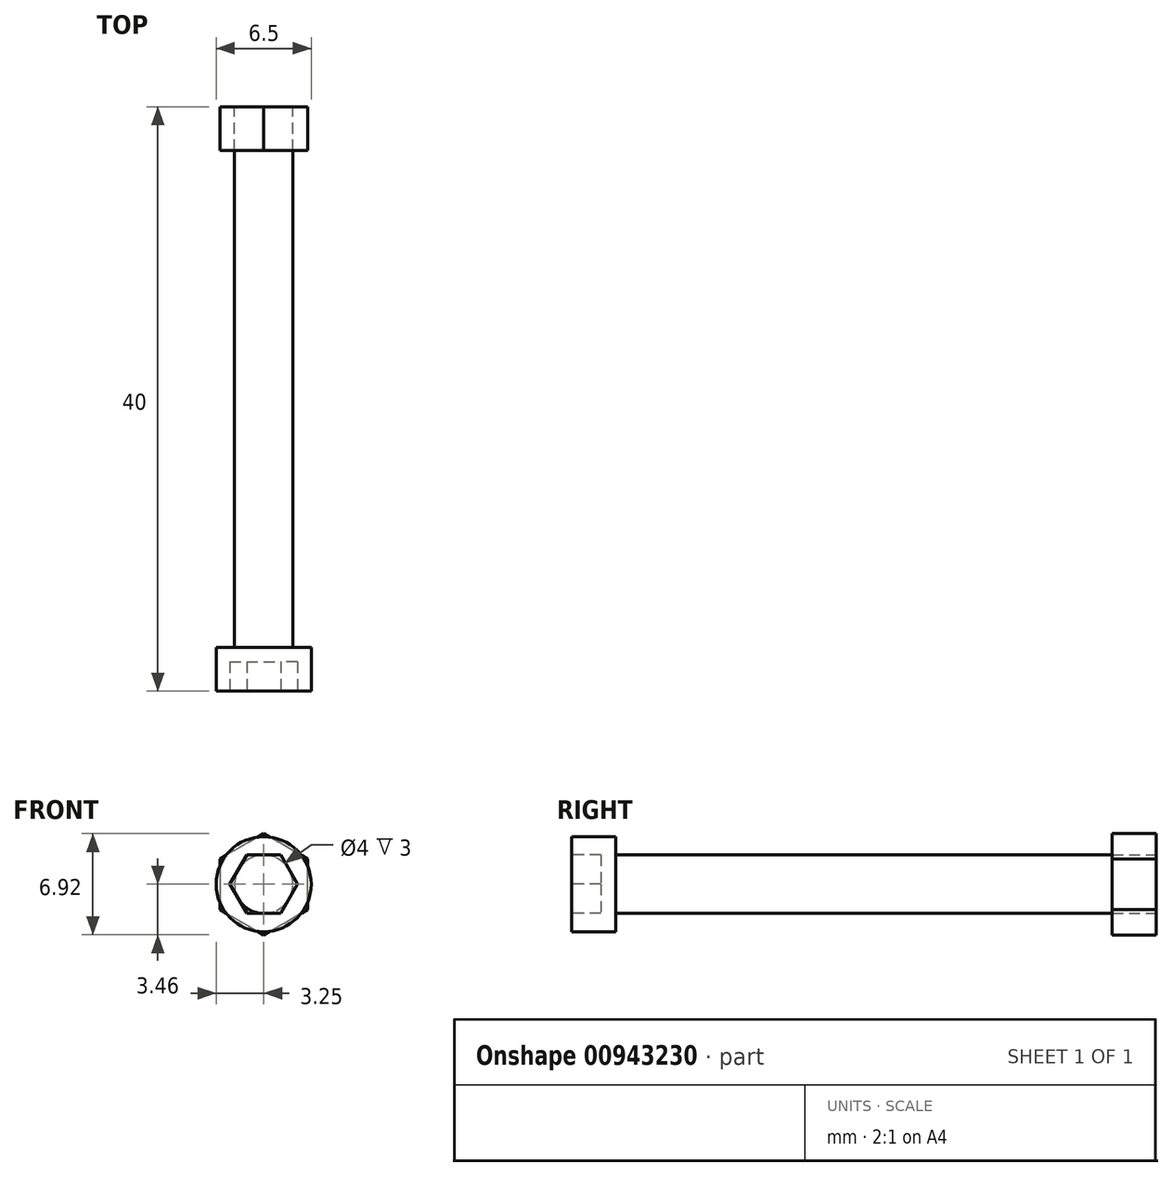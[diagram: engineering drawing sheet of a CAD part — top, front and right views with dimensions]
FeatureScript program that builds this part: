
annotation { "Feature Type Name" : "Feature", "Feature Type Description" : "" }
export const myFeature = defineFeature(function(context is Context, id is Id, definition is map)
    precondition{}
    {
        {
            var Q0;
            Q0=qCreatedBy(makeId("Front.planeOp"),FACE);
            var sketch = newSketch(context, id + "F0", { "sketchPlane" : qUnion([Q0])});
            skCircle(sketch, "E0", {"center": v(0, 0) * mm, "radius": 2 * mm});
            skSolve(sketch);
        }
        {
            var Q0;
            Q0=makeQuery(id+"F0.imprint","IMPRINT",FACE,{"disambiguationData":[TD([[makeQuery(id+"F0.imprint","IMPRINT",EDGE,{"derivedFrom":sQuery(id+"F0.wireOp",EDGE,"E0")}),1.0]])]});
            extrude(context, id + "F1", {"entities" : qUnion([Q0]), "depth" : 37 * mm, "offsetDistance" : 25 * mm, "symmetric" : true});
        }
        {
            var Q0;
            Q0=makeQuery(id+"F1.opExtrude","CAP_FACE",FACE,{"disambiguationData":[OSD([sQuery(id+"F0.wireOp",EDGE,"E0")])],"isStart":false});
            var sketch = newSketch(context, id + "F2", { "sketchPlane" : qUnion([Q0])});
            skCircle(sketch, "E1", {"center": v(0, 0) * mm, "radius": 3.25 * mm});
            skSolve(sketch);
        }
        {
            var Q0;
            Q0=makeQuery(id+"F2.imprint","IMPRINT",FACE,{"disambiguationData":[TD([[makeQuery(id+"F2.imprint","IMPRINT",EDGE,{"derivedFrom":sQuery(id+"F2.wireOp",EDGE,"E1")}),1.0]])]});
            var Q1;
            Q1=makeQuery(id+"F2.imprint","IMPRINT",FACE,{"disambiguationData":[TD([[makeQuery(id+"F2.imprint","IMPRINT",EDGE,{"derivedFrom":makeQuery(id+"F1.opExtrude","CAP_EDGE",EDGE,{"disambiguationData":[OSD([sQuery(id+"F0.wireOp",EDGE,"E0")])],"isStart":false})}),1.0]])]});
            extrude(context, id + "F3", {"entities" : qUnion([Q0, Q1]), "operationType" : NewBodyOperationType.ADD, "depth" : 3 * mm, "offsetDistance" : 25 * mm});
        }
        {
            var Q0;
            Q0=makeQuery(id+"F3.opExtrude","CAP_FACE",FACE,{"disambiguationData":[OSD([sQuery(id+"F2.wireOp",EDGE,"E1")])],"isStart":false});
            var sketch = newSketch(context, id + "F4", { "sketchPlane" : qUnion([Q0])});
            skCircle(sketch, "E2.cCircle", {"center": v(0, 0) * mm, "radius": 2 * mm, "construction": true});
            skLineSegment(sketch, "E2.0", {"start": v(2.3, 0) * mm, "end": v(1.15, -2) * mm});
            skLineSegment(sketch, "E2.1", {"start": v(1.15, -2) * mm, "end": v(-1.15, -2) * mm});
            skLineSegment(sketch, "E2.2", {"start": v(-1.15, -2) * mm, "end": v(-2.3, 0) * mm});
            skLineSegment(sketch, "E2.3", {"start": v(-2.3, 0) * mm, "end": v(-1.15, 2) * mm});
            skLineSegment(sketch, "E2.4", {"start": v(-1.15, 2) * mm, "end": v(1.15, 2) * mm});
            skLineSegment(sketch, "E2.5", {"start": v(1.15, 2) * mm, "end": v(2.3, 0) * mm});
            skPoint(sketch, "E2.0.midPoint", {"position": v(1.73, -1) * mm});
            skLineSegment(sketch, "E3", {"start": v(0, 0) * mm, "end": v(0.92, 0) * mm, "construction": true});
            skSolve(sketch);
        }
        {
            var Q0;
            Q0=makeQuery(id+"F4.imprint","IMPRINT",FACE,{"disambiguationData":[TD([[makeQuery(id+"F4.imprint","IMPRINT",EDGE,{"derivedFrom":sQuery(id+"F4.wireOp",EDGE,"E2.0")}),-1.0]])]});
            extrude(context, id + "F5", {"entities" : qUnion([Q0]), "operationType" : NewBodyOperationType.REMOVE, "oppositeDirection" : true, "depth" : 2 * mm, "offsetDistance" : 25 * mm});
        }
        {
            var Q0;
            Q0=makeQuery(id+"F1.opExtrude","CAP_FACE",FACE,{"disambiguationData":[OSD([sQuery(id+"F0.wireOp",EDGE,"E0")])],"isStart":true});
            var sketch = newSketch(context, id + "F6", { "sketchPlane" : qUnion([Q0])});
            skCircle(sketch, "E4", {"center": v(0, 0) * mm, "radius": 2 * mm});
            skCircle(sketch, "E5.cCircle", {"center": v(0, 0) * mm, "radius": 3 * mm, "construction": true});
            skLineSegment(sketch, "E5.0", {"start": v(0, 3.46) * mm, "end": v(3, 1.73) * mm});
            skLineSegment(sketch, "E5.1", {"start": v(3, 1.73) * mm, "end": v(3, -1.73) * mm});
            skLineSegment(sketch, "E5.2", {"start": v(3, -1.73) * mm, "end": v(0, -3.46) * mm});
            skLineSegment(sketch, "E5.3", {"start": v(0, -3.46) * mm, "end": v(-3, -1.73) * mm});
            skLineSegment(sketch, "E5.4", {"start": v(-3, -1.73) * mm, "end": v(-3, 1.73) * mm});
            skLineSegment(sketch, "E5.5", {"start": v(-3, 1.73) * mm, "end": v(0, 3.46) * mm});
            skPoint(sketch, "E5.0.midPoint", {"position": v(1.5, 2.6) * mm});
            skLineSegment(sketch, "E6", {"start": v(0, 0) * mm, "end": v(0, 0.95) * mm, "construction": true});
            skSolve(sketch);
        }
        {
            var Q0;
            Q0=makeQuery(id+"F6.imprint","IMPRINT",FACE,{"disambiguationData":[TD([[makeQuery(id+"F6.imprint","IMPRINT",EDGE,{"derivedFrom":sQuery(id+"F6.wireOp",EDGE,"E4")}),1.0]])]});
            extrude(context, id + "F7", {"entities" : qUnion([Q0]), "oppositeDirection" : true, "depth" : 3 * mm, "offsetDistance" : 25 * mm});
        }
    });
